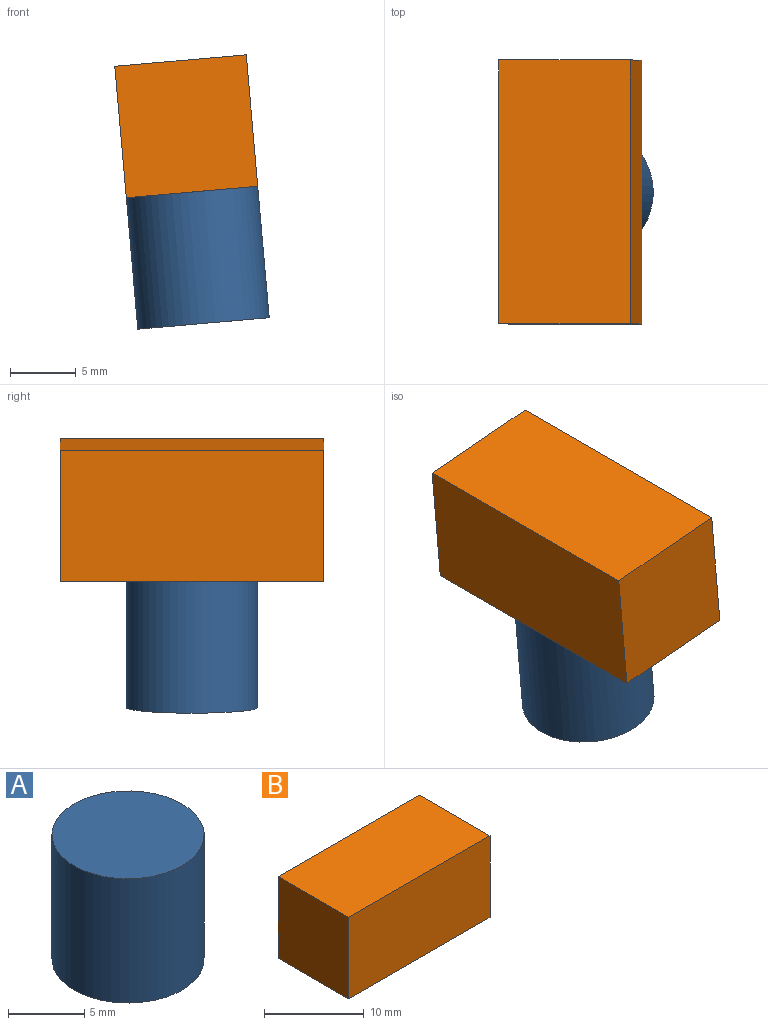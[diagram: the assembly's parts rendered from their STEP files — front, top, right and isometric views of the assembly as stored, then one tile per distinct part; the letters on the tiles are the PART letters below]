
ASSEMBLY  parts=2 mates=3
PART A: 3 faces, bbox 10x10x10 mm
  f0: cylinder r=5mm len=10mm, axis (0,0,-1), area 314.2mm2, adj f1,f2
  f1: plane 10x10mm, normal (0,0,1), area 78.5mm2, adj f0
  f2: plane 10x10mm, normal (0,0,-1), area 78.5mm2, adj f0
PART B: 6 faces, bbox 20x10x10 mm
  f0: plane 10x10mm, normal (1,0,0), area 100mm2, adj f1,f3,f4,f5
  f1: plane 20x10mm, normal (0,1,0), area 200mm2, adj f0,f2,f4,f5
  f2: plane 10x10mm, normal (-1,0,0), area 100mm2, adj f1,f3,f4,f5
  f3: plane 20x10mm, normal (0,-1,0), area 200mm2, adj f0,f2,f4,f5
  f4: plane 20x10mm, normal (0,0,1), area 200mm2, adj f0,f1,f2,f3
  f5: plane 20x10mm, normal (0,0,-1), area 200mm2, adj f0,f1,f2,f3
PLACE A rot(axis=(-0.04,-0.04,1),90.1deg) t=(-14.58,-26.55,-12.23)mm
PLACE B rot(axis=(-0.04,-0.04,1),90.1deg) t=(-15.45,-26.55,-2.27)mm
MATE fastened B.f5 <-> A.f0  axis (0.09,0,-1) through (-15.45,-26.55,-2.27)mm
MATE parallel A.f0 <-> B.f5  axis (-0.09,0,1) through (-15.45,-26.55,-2.27)mm
MATE slider A.f0 <-> B.f5  axis (-0.09,0,1) through (-15.45,-26.55,-2.27)mm
